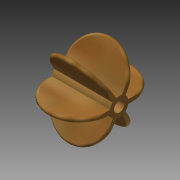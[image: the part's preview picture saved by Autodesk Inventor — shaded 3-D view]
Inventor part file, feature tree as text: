
AUTODESK INVENTOR PART (.ipt)
format: ipt  version: 2015 (Build 190159000, 159)  size: 244,736 bytes
history: native  units: mm
features: extrude x3, sketch x3, pattern_circular x1, fillet x1
ambient origin geometry x8: Origin, YZ Plane, XZ Plane, XY Plane, X Axis, Y Axis, Z Axis, Center Point
bodies: 实体1 (feature_tree)
feature tree (8):
  extrude  "拉伸1"  Depth=28.0mm
  pattern_circular  "环形阵列1"  [2 undecoded]
  extrude  "拉伸2"  Depth=1.0mm TaperAngle=360.0deg
  extrude  "拉伸3"  Depth=1.0mm
  fillet  "圆角2"  Radius=28.0mm
  sketch  "草图1"  dims[d0=28.0mm d1=20.0mm]
  sketch  "草图2"  dims[d3=14.8mm]
  sketch  "草图3"  dims[d4=14.8mm d5=2.0mm d6=0.0mm d8=60.0mm d9=360.0deg d11=9.0mm d12=28.0mm d13=0.0mm d14=5.0mm d15=5.0mm d16=0.0mm d17=1.0mm]
note: 2 required parameter values undecoded (feature->parameter linkage not recoverable at this tier; creation-order binding heuristic only, values carry confidence <= 0.55)
